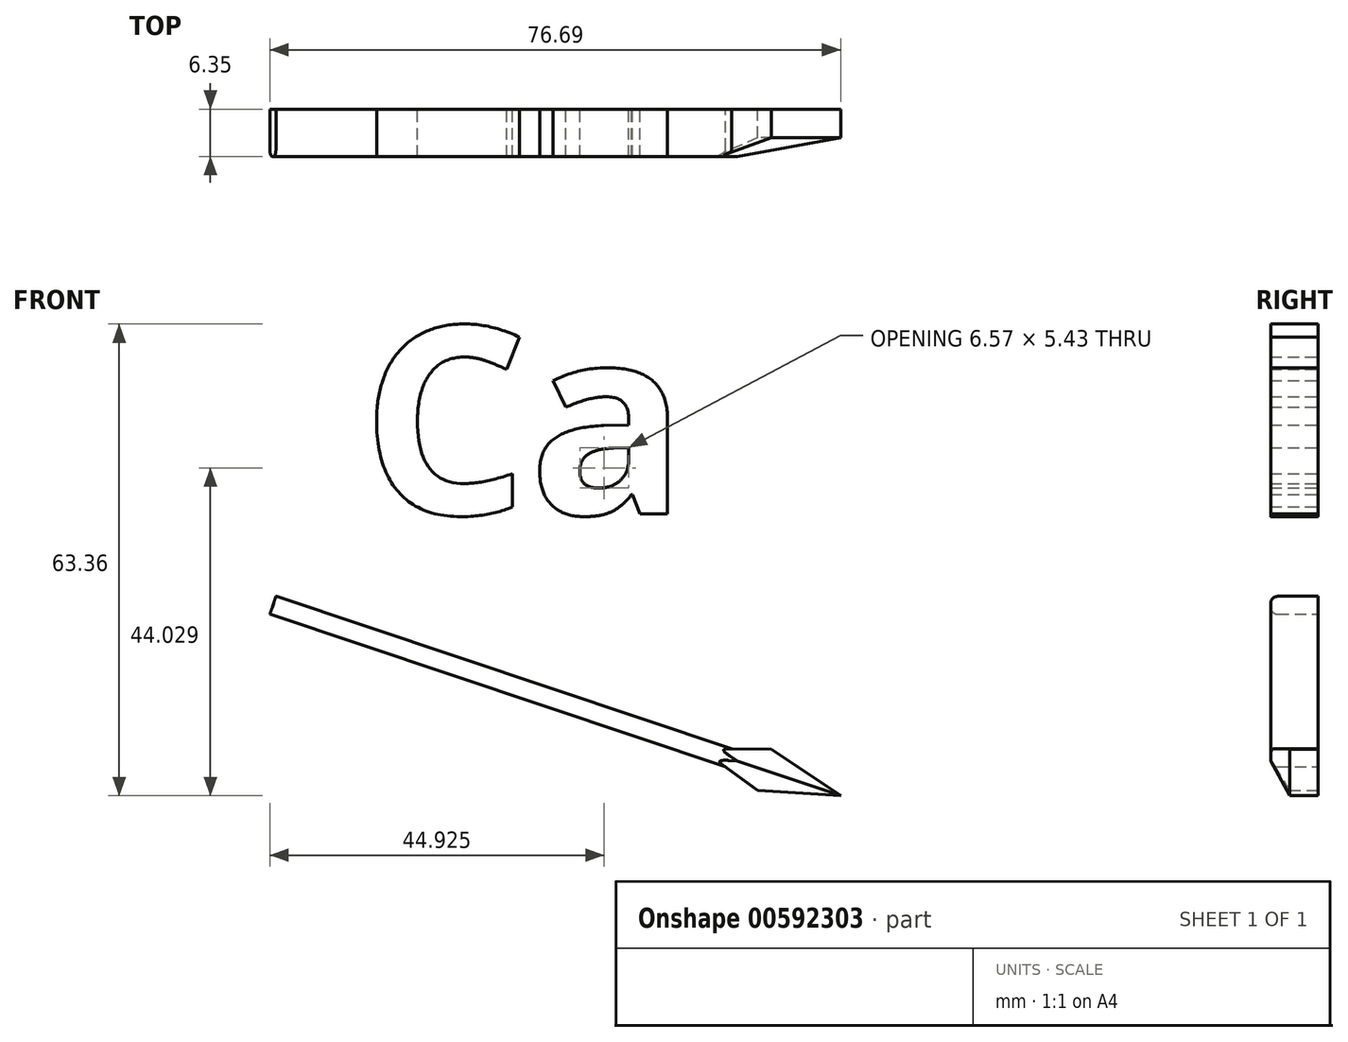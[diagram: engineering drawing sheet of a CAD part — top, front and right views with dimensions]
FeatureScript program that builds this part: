
annotation { "Feature Type Name" : "Feature", "Feature Type Description" : "" }
export const myFeature = defineFeature(function(context is Context, id is Id, definition is map)
    precondition{}
    {
        {
            var Q0;
            Q0=qCreatedBy(makeId("Front.planeOp"),FACE);
            var sketch = newSketch(context, id + "F0", { "sketchPlane" : qUnion([Q0])});
            skText(sketch, "E0", { "text": "Ca", "fontName": "OpenSans-Bold.ttf"});
            skLineSegment(sketch, "E1", {"start": v(-26.78, 5.35) * mm, "end": v(34.45, -15.16) * mm});
            skLineSegment(sketch, "E2", {"start": v(34.45, -15.16) * mm, "end": v(33.64, -17.58) * mm});
            skLineSegment(sketch, "E3", {"start": v(33.64, -17.58) * mm, "end": v(-27.6, 2.94) * mm});
            skLineSegment(sketch, "E4", {"start": v(-26.78, 5.35) * mm, "end": v(-27.6, 2.94) * mm});
            skLineSegment(sketch, "E5", {"start": v(34.45, -15.16) * mm, "end": v(39.8, -15.23) * mm});
            skLineSegment(sketch, "E6", {"start": v(34.04, -16.37) * mm, "end": v(49.1, -21.42) * mm});
            skLineSegment(sketch, "E7", {"start": v(39.8, -15.23) * mm, "end": v(49.1, -21.42) * mm});
            skLineSegment(sketch, "E8.MirrorCS", {"start": v(37.94, -20.75) * mm, "end": v(49.1, -21.42) * mm});
            skLineSegment(sketch, "E9.MirrorCS", {"start": v(33.64, -17.58) * mm, "end": v(37.94, -20.75) * mm});
            const initialGuessF0  = {"E0": [-0.0153, 0.0164, 1, 0, 0.0254]};
            skSetInitialGuess(sketch, initialGuessF0);
            skSolve(sketch);
        }
        {
            var Q0;
            Q0=makeQuery(id+"F0.imprint","IMPRINT",FACE,{"disambiguationData":[TD([[makeQuery(id+"F0.imprint","IMPRINT",EDGE,{"derivedFrom":sQuery(id+"F0.wireOp",EDGE,"E0.sketch_text.stroke-0")}),-1.0]])]});
            var Q1;
            Q1=makeQuery(id+"F0.imprint","IMPRINT",FACE,{"disambiguationData":[TD([[makeQuery(id+"F0.imprint","IMPRINT",EDGE,{"derivedFrom":sQuery(id+"F0.wireOp",EDGE,"E0.sketch_text.stroke-15")}),-1.0]])]});
            var Q2;
            {var subQ3=sQuery(id+"F0.wireOp",EDGE,"E1");Q2=makeQuery(id+"F0.imprint","IMPRINT",FACE,{"disambiguationData":[TD([[makeQuery(id+"F0.imprint","IMPRINT",EDGE,{"derivedFrom":subQ3}),-1.0]])]});}
            extrude(context, id + "F1", {"entities" : qUnion([Q0, Q1, Q2]), "depth" : 6.35 * mm, "offsetDistance" : 25.4 * mm});
        }
        {
            var Q0;
            {var subQ0=sQuery(id+"F0.wireOp",EDGE,"E5");Q0=makeQuery(id+"F0.imprint","IMPRINT",FACE,{"disambiguationData":[TD([[makeQuery(id+"F0.imprint","IMPRINT",EDGE,{"derivedFrom":subQ0}),-1.0]])]});}
            var Q1;
            {var subQ2=sQuery(id+"F0.wireOp",EDGE,"E6");Q1=makeQuery(id+"F0.imprint","IMPRINT",FACE,{"disambiguationData":[TD([[makeQuery(id+"F0.imprint","IMPRINT",EDGE,{"derivedFrom":subQ2}),-1.0]])]});}
            extrude(context, id + "F2", {"entities" : qUnion([Q0, Q1]), "operationType" : NewBodyOperationType.ADD, "depth" : 6.35 * mm, "offsetDistance" : 25.4 * mm});
        }
        {
            var Q0;
            Q0=makeQuery(id+"F2.opExtrude","CAP_EDGE",EDGE,{"disambiguationData":[OSD([sQuery(id+"F0.wireOp",EDGE,"E8.MirrorCS")])],"isStart":false});
            var Q1;
            Q1=makeQuery(id+"F2.opExtrude","CAP_EDGE",EDGE,{"disambiguationData":[OSD([sQuery(id+"F0.wireOp",EDGE,"E7")])],"isStart":false});
            chamfer(context, id + "F3", {"entities" : qUnion([Q0, Q1]), "chamferType" : ChamferType.TWO_OFFSETS, "width1" : 2.54 * mm, "oppositeDirection" : true, "width2" : 3.8 * mm});
        }
        {
            var Q0;
            Q0=makeQuery(id+"F1.opExtrude","CAP_EDGE",EDGE,{"disambiguationData":[OSD([sQuery(id+"F0.wireOp",EDGE,"E1")])],"isStart":false});
            var Q1;
            Q1=makeQuery(id+"F1.opExtrude","CAP_EDGE",EDGE,{"disambiguationData":[OSD([sQuery(id+"F0.wireOp",EDGE,"E3")])],"isStart":false});
            fillet(context, id + "F4", {"entities" : qUnion([Q0, Q1]), "radius" : 0.95 * mm, "tangentPropagation" : true, "allowEdgeOverflow" : false});
        }
    });
